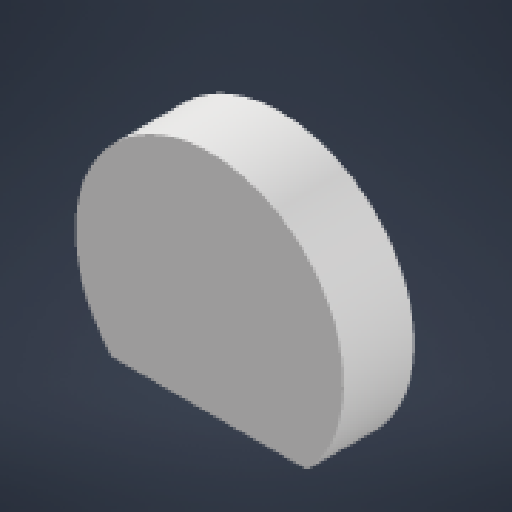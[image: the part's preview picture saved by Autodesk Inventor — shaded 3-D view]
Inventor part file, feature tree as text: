
AUTODESK INVENTOR PART (.ipt)
format: ipt  version: 2024 (Build 280153000, 153)  size: 126,976 bytes
history: native  units: in
note: dims shown in document units (in); Inventor stores cm internally (conversion verified against a paired STEP export)
features: other x3, extrude x2, sketch x2, reference x1, projected_geometry x1
ambient origin geometry x8: Origin, YZ Plane, XZ Plane, XY Plane, X Axis, Y Axis, Z Axis, Center Point
bodies: Solid1 (feature_tree)
feature tree (9):
  extrude  "Extrusion1"  Depth=12.0in
  extrude  "Extrusion2"  [1 undecoded]
  sketch  "Sketch1"  dims[d0=1.0in d1=0.0in d3=12.0in]
  reference  "Reference1"
  sketch  "Sketch2"  dims[d4=3.1496in d5=0.0in]
  projected_geometry  "Projected Loop1"
  other  "<userpath>\Desktop\Camera_Mount.iam"
  other  "Camera_Mount.iam"
  other  "Head_Baseplate:1"
note: 1 required parameter value undecoded (feature->parameter linkage not recoverable at this tier; creation-order binding heuristic only, values carry confidence <= 0.55)
